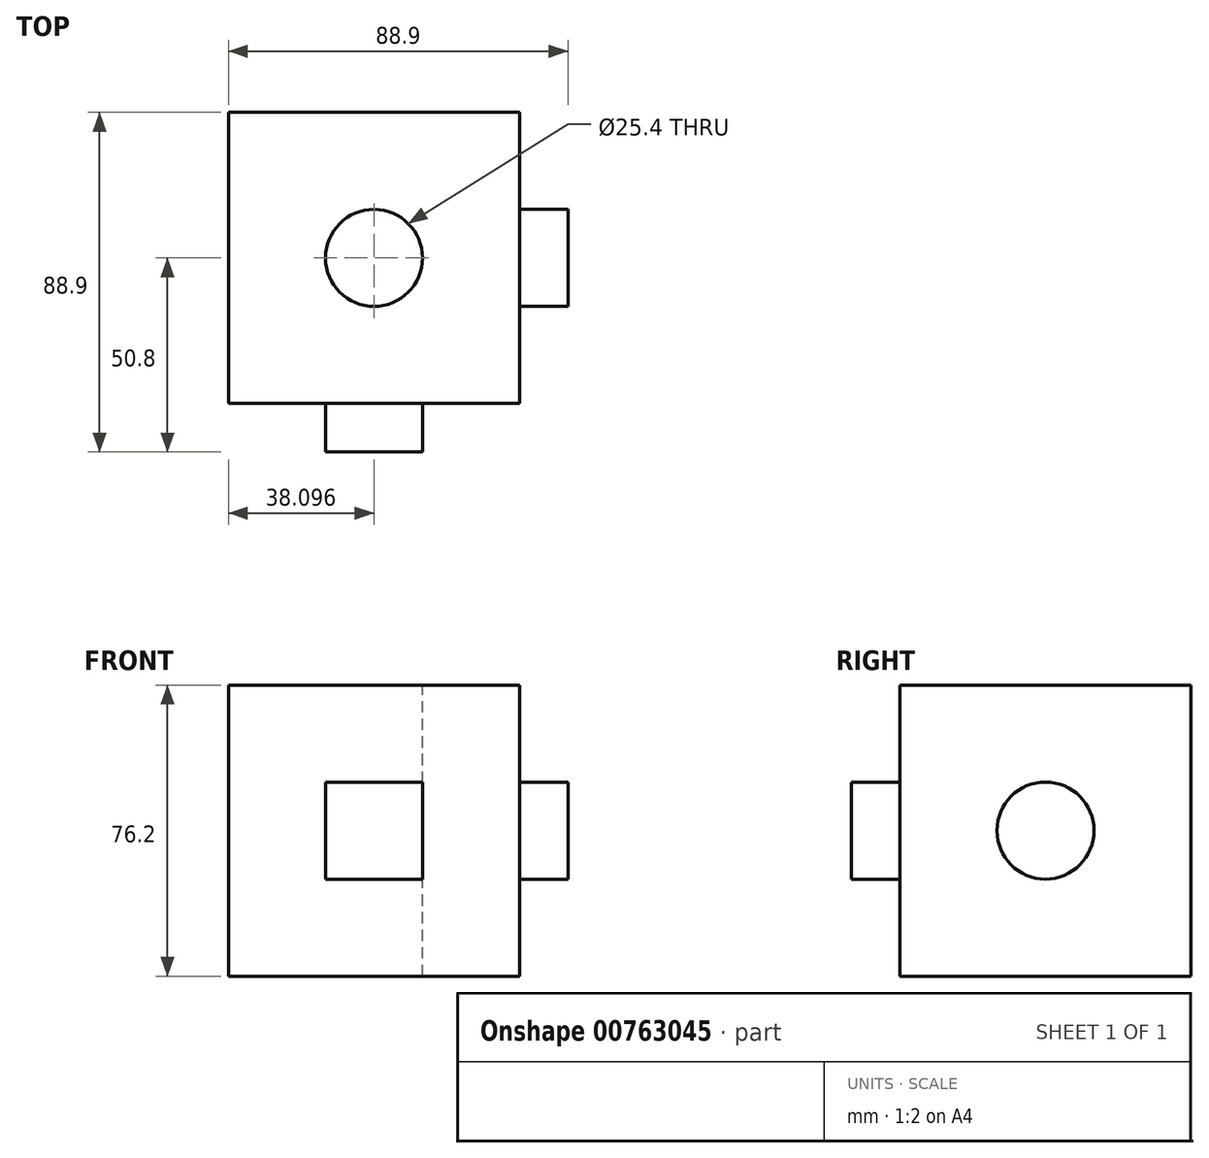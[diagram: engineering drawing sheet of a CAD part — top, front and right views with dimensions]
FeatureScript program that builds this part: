
annotation { "Feature Type Name" : "Feature", "Feature Type Description" : "" }
export const myFeature = defineFeature(function(context is Context, id is Id, definition is map)
    precondition{}
    {
        {
            var Q0;
            Q0=qCreatedBy(makeId("Front.planeOp"),FACE);
            var sketch = newSketch(context, id + "F0", { "sketchPlane" : qUnion([Q0])});
            skLineSegment(sketch, "E0.bottom", {"start": v(-67.6, 27.32) * mm, "end": v(8.6, 27.32) * mm});
            skLineSegment(sketch, "E0.top", {"start": v(-67.6, -48.88) * mm, "end": v(8.6, -48.88) * mm});
            skLineSegment(sketch, "E0.left", {"start": v(-67.6, 27.32) * mm, "end": v(-67.6, -48.88) * mm});
            skLineSegment(sketch, "E0.right", {"start": v(8.6, 27.32) * mm, "end": v(8.6, -48.88) * mm});
            skSolve(sketch);
        }
        {
            var Q0;
            Q0=makeQuery(id+"F0.imprint","IMPRINT",FACE,{"disambiguationData":[TD([[makeQuery(id+"F0.imprint","IMPRINT",EDGE,{"derivedFrom":sQuery(id+"F0.wireOp",EDGE,"E0.bottom")}),-1.0]])]});
            extrude(context, id + "F1", {"entities" : qUnion([Q0]), "depth" : 76.2 * mm, "offsetDistance" : 25.4 * mm});
        }
        {
            var Q0;
            Q0=makeQuery(id+"F1.opExtrude","SWEPT_FACE",FACE,{"disambiguationData":[OSD([sQuery(id+"F0.wireOp",EDGE,"E0.right")])]});
            var sketch = newSketch(context, id + "F2", { "sketchPlane" : qUnion([Q0])});
            skCircle(sketch, "E1", {"center": v(-38.1, -10.78) * mm, "radius": 12.7 * mm});
            skSolve(sketch);
        }
        {
            var Q0;
            Q0=makeQuery(id+"F2.imprint","IMPRINT",FACE,{"disambiguationData":[TD([[makeQuery(id+"F2.imprint","IMPRINT",EDGE,{"derivedFrom":sQuery(id+"F2.wireOp",EDGE,"E1")}),1.0]])]});
            extrude(context, id + "F3", {"entities" : qUnion([Q0]), "operationType" : NewBodyOperationType.ADD, "depth" : 12.7 * mm, "offsetDistance" : 25.4 * mm});
        }
        {
            var Q0;
            Q0=makeQuery(id+"F1.opExtrude","SWEPT_FACE",FACE,{"disambiguationData":[OSD([sQuery(id+"F0.wireOp",EDGE,"E0.bottom")])]});
            var sketch = newSketch(context, id + "F4", { "sketchPlane" : qUnion([Q0])});
            skPoint(sketch, "E2", {"position": v(-29.5, -38.1) * mm});
            skSolve(sketch);
        }
        {
            var Q0;
            Q0=makeQuery(id+"F1.opExtrude","CAP_FACE",FACE,{"disambiguationData":[OSD([sQuery(id+"F0.wireOp",EDGE,"E0.bottom"),sQuery(id+"F0.wireOp",EDGE,"E0.top"),sQuery(id+"F0.wireOp",EDGE,"E0.left"),sQuery(id+"F0.wireOp",EDGE,"E0.right")])],"isStart":false});
            var sketch = newSketch(context, id + "F5", { "sketchPlane" : qUnion([Q0])});
            skLineSegment(sketch, "E3.bottom", {"start": v(-42.2, 1.92) * mm, "end": v(-16.8, 1.92) * mm});
            skLineSegment(sketch, "E3.top", {"start": v(-42.2, -23.48) * mm, "end": v(-16.8, -23.48) * mm});
            skLineSegment(sketch, "E3.left", {"start": v(-42.2, 1.92) * mm, "end": v(-42.2, -23.48) * mm});
            skLineSegment(sketch, "E3.right", {"start": v(-16.8, 1.92) * mm, "end": v(-16.8, -23.48) * mm});
            skSolve(sketch);
        }
        {
            var Q0;
            Q0=makeQuery(id+"F5.imprint","IMPRINT",FACE,{"disambiguationData":[TD([[makeQuery(id+"F5.imprint","IMPRINT",EDGE,{"derivedFrom":sQuery(id+"F5.wireOp",EDGE,"E3.bottom")}),-1.0]])]});
            extrude(context, id + "F6", {"entities" : qUnion([Q0]), "operationType" : NewBodyOperationType.ADD, "depth" : 12.7 * mm, "offsetDistance" : 25.4 * mm});
        }
        {
            var Q0;
            Q0=sQuery(id+"F4.wireOp",VERTEX,"E2");
            var Q1;
            Q1=makeQuery(id+"F1.opExtrude","SWEPT_BODY",BODY,{"disambiguationData":[OSD([sQuery(id+"F0.wireOp",EDGE,"E0.bottom"),sQuery(id+"F0.wireOp",EDGE,"E0.top"),sQuery(id+"F0.wireOp",EDGE,"E0.left"),sQuery(id+"F0.wireOp",EDGE,"E0.right")])]});
            hole(context, id + "F7", {"style" : HoleStyle.SIMPLE, "endStyle" : HoleEndStyle.THROUGH, "holeDiameter" : 25.4 * mm, "majorDiameter" : 6.35 * mm, "isTappedThrough" : true, "tappedDepth" : 12.7 * mm, "tapClearance" : 3, "locations" : qUnion([Q0]), "scope" : qUnion([Q1])});
        }
    });
